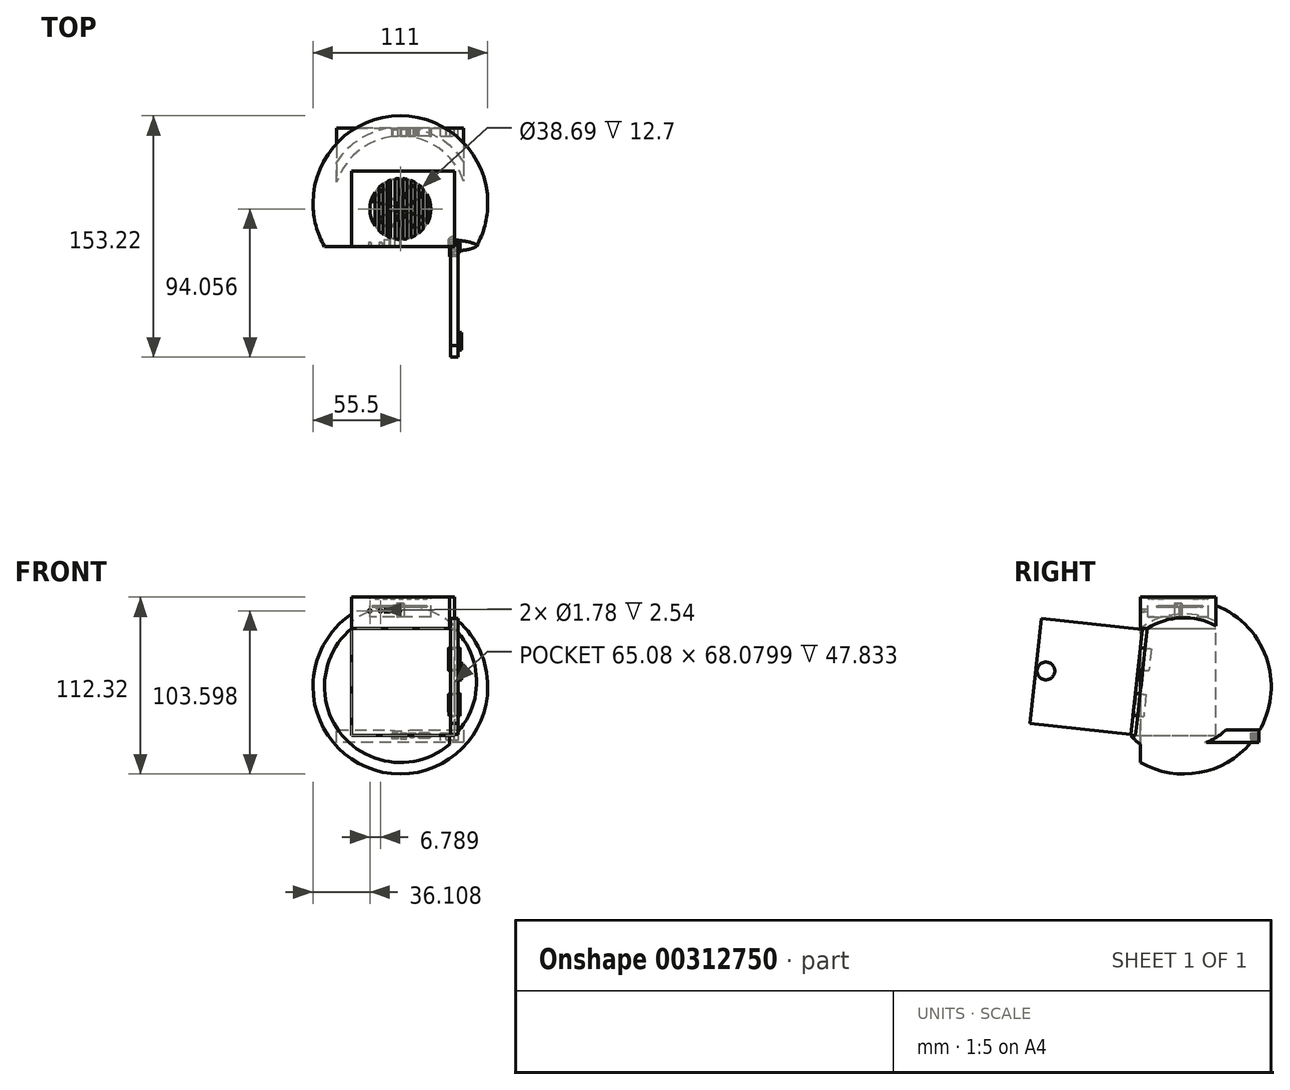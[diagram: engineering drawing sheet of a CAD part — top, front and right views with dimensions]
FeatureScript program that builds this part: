
annotation { "Feature Type Name" : "Feature", "Feature Type Description" : "" }
export const myFeature = defineFeature(function(context is Context, id is Id, definition is map)
    precondition{}
    {
        {
            var Q0;
            Q0=qCreatedBy(makeId("Front.planeOp"),FACE);
            var sketch = newSketch(context, id + "F0", { "sketchPlane" : qUnion([Q0])});
            skArc(sketch, "E0", {"start": v(55.5, 0) * mm, "mid": v(0, 55.5) * mm, "end": v(-55.5, 0) * mm});
            skLineSegment(sketch, "E1", {"start": v(-55.5, 0) * mm, "end": v(55.5, 0) * mm});
            skSolve(sketch);
        }
        {
            var Q0;
            Q0 = qSketchRegion(id + "F0", true);
            var Q1;
            Q1=sQuery(id+"F0.wireOp",EDGE,"E1");
            revolve(context, id + "F1", {"entities" : qUnion([Q0]), "axis" : qUnion([Q1]), "revolveType" : RevolveType.FULL});
        }
        {
            var Q0;
            Q0=qCreatedBy(makeId("Front.planeOp"),FACE);
            var sketch = newSketch(context, id + "F2", { "sketchPlane" : qUnion([Q0])});
            skLineSegment(sketch, "E2", {"start": v(-30.83, 37.01) * mm, "end": v(34.25, 37.01) * mm});
            skLineSegment(sketch, "E3", {"start": v(34.25, 37.01) * mm, "end": v(34.25, -31.07) * mm});
            skLineSegment(sketch, "E4", {"start": v(34.25, -31.07) * mm, "end": v(-30.83, -31.07) * mm});
            skLineSegment(sketch, "E5", {"start": v(-30.83, -31.07) * mm, "end": v(-30.83, 37.01) * mm});
            skLineSegment(sketch, "E6", {"start": v(-56.39, 0) * mm, "end": v(59.8, 0) * mm});
            skSolve(sketch);
        }
        {
            var Q0;
            Q0=qCreatedBy(makeId("Front.planeOp"),FACE);
            var sketch = newSketch(context, id + "F3", { "sketchPlane" : qUnion([Q0])});
            skLineSegment(sketch, "E7", {"start": v(40.18, -35.57) * mm, "end": v(-40.42, -35.57) * mm});
            skLineSegment(sketch, "E8", {"start": v(-40.42, -35.57) * mm, "end": v(-40.42, -27.54) * mm});
            skLineSegment(sketch, "E9", {"start": v(-40.42, -27.54) * mm, "end": v(40.18, -27.54) * mm});
            skLineSegment(sketch, "E10", {"start": v(40.18, -27.54) * mm, "end": v(40.18, -35.57) * mm});
            skSolve(sketch);
        }
        {
            var Q0;
            Q0 = qSketchRegion(id + "F3", true);
            extrude(context, id + "F4", {"entities" : qUnion([Q0]), "operationType" : NewBodyOperationType.ADD, "oppositeDirection" : true, "depth" : 47.75 * mm});
        }
        {
            var Q0;
            Q0=makeQuery(id+"F4.opExtrude","CAP_FACE",FACE,{"disambiguationData":[OSD([sQuery(id+"F3.wireOp",EDGE,"E7"),sQuery(id+"F3.wireOp",EDGE,"E8"),sQuery(id+"F3.wireOp",EDGE,"E9"),sQuery(id+"F3.wireOp",EDGE,"E10")])],"isStart":false});
            var sketch = newSketch(context, id + "F5", { "sketchPlane" : qUnion([Q0])});
            skLineSegment(sketch, "E11", {"start": v(-36.59, -29.3) * mm, "end": v(-36.59, -34.19) * mm});
            skLineSegment(sketch, "E12", {"start": v(-36.59, -34.19) * mm, "end": v(-25.65, -34.19) * mm});
            skLineSegment(sketch, "E13", {"start": v(-25.65, -34.19) * mm, "end": v(-25.65, -29.3) * mm});
            skLineSegment(sketch, "E14", {"start": v(-25.65, -29.3) * mm, "end": v(-36.59, -29.3) * mm});
            skLineSegment(sketch, "E15", {"start": v(-18.62, -29.3) * mm, "end": v(-11.86, -29.3) * mm});
            skLineSegment(sketch, "E16", {"start": v(-11.86, -29.3) * mm, "end": v(-11.86, -30.02) * mm});
            skLineSegment(sketch, "E17", {"start": v(-18.62, -29.3) * mm, "end": v(-18.62, -30.02) * mm});
            skLineSegment(sketch, "E18.MirrorCS", {"start": v(-18.62, -32.85) * mm, "end": v(-18.62, -32.11) * mm});
            skLineSegment(sketch, "E19.MirrorCS", {"start": v(-18.62, -32.85) * mm, "end": v(-11.86, -32.85) * mm});
            skLineSegment(sketch, "E20.MirrorCS", {"start": v(-11.86, -32.85) * mm, "end": v(-11.86, -32.11) * mm});
            skArc(sketch, "E21", {"start": v(-18.62, -30.02) * mm, "mid": v(-19.7, -31.07) * mm, "end": v(-18.62, -32.11) * mm});
            skArc(sketch, "E22", {"start": v(-11.86, -32.11) * mm, "mid": v(-10.83, -31.07) * mm, "end": v(-11.86, -30.02) * mm});
            skLineSegment(sketch, "E23", {"start": v(-9.63, -29.3) * mm, "end": v(-9.63, -31.07) * mm});
            skLineSegment(sketch, "E24", {"start": v(-9.63, -31.07) * mm, "end": v(-8.36, -31.07) * mm});
            skLineSegment(sketch, "E25", {"start": v(-8.36, -31.07) * mm, "end": v(-8.36, -32.5) * mm});
            skLineSegment(sketch, "E26", {"start": v(-8.36, -32.5) * mm, "end": v(-6.57, -32.5) * mm});
            skLineSegment(sketch, "E27", {"start": v(-6.57, -32.5) * mm, "end": v(-6.57, -31.07) * mm});
            skLineSegment(sketch, "E28", {"start": v(-6.57, -31.07) * mm, "end": v(-5.3, -31.07) * mm});
            skLineSegment(sketch, "E29", {"start": v(-5.3, -31.07) * mm, "end": v(-5.3, -29.3) * mm});
            skLineSegment(sketch, "E30", {"start": v(-5.3, -29.3) * mm, "end": v(-9.63, -29.3) * mm});
            skLineSegment(sketch, "E31", {"start": v(-3.85, -29.3) * mm, "end": v(-3.85, -31.07) * mm});
            skLineSegment(sketch, "E32", {"start": v(-3.85, -31.07) * mm, "end": v(0, -31.07) * mm});
            skLineSegment(sketch, "E33", {"start": v(0, -31.07) * mm, "end": v(0, -29.3) * mm});
            skLineSegment(sketch, "E34", {"start": v(0, -29.3) * mm, "end": v(-3.85, -29.3) * mm});
            skLineSegment(sketch, "E35", {"start": v(1.49, -31.07) * mm, "end": v(1.49, -29.3) * mm});
            skLineSegment(sketch, "E36", {"start": v(1.49, -29.3) * mm, "end": v(5.28, -29.3) * mm});
            skLineSegment(sketch, "E37", {"start": v(5.28, -29.3) * mm, "end": v(5.28, -31.07) * mm});
            skLineSegment(sketch, "E38", {"start": v(5.28, -31.07) * mm, "end": v(1.49, -31.07) * mm});
            skLineSegment(sketch, "E39", {"start": v(-3.85, -31.55) * mm, "end": v(0, -31.55) * mm});
            skLineSegment(sketch, "E40", {"start": v(0, -31.55) * mm, "end": v(0, -33.32) * mm});
            skLineSegment(sketch, "E41", {"start": v(0, -33.32) * mm, "end": v(-3.85, -33.32) * mm});
            skLineSegment(sketch, "E42", {"start": v(-3.85, -33.32) * mm, "end": v(-3.85, -31.55) * mm});
            skLineSegment(sketch, "E43", {"start": v(1.49, -31.55) * mm, "end": v(1.49, -33.32) * mm});
            skLineSegment(sketch, "E44", {"start": v(1.49, -33.32) * mm, "end": v(5.28, -33.32) * mm});
            skLineSegment(sketch, "E45", {"start": v(5.28, -33.32) * mm, "end": v(5.28, -31.55) * mm});
            skLineSegment(sketch, "E46", {"start": v(5.28, -31.55) * mm, "end": v(1.49, -31.55) * mm});
            skSolve(sketch);
        }
        {
            var Q0;
            Q0 = qSketchRegion(id + "F5", true);
            extrude(context, id + "F6", {"entities" : qUnion([Q0]), "operationType" : NewBodyOperationType.REMOVE, "oppositeDirection" : true, "depth" : 5.08 * mm});
        }
        {
            var Q0;
            Q0=makeQuery(id+"F6.boolean.opBoolean","COPY",FACE,{"derivedFrom":makeQuery(id+"F6.opExtrude","CAP_FACE",FACE,{"disambiguationData":[OSD([sQuery(id+"F5.wireOp",EDGE,"E11"),sQuery(id+"F5.wireOp",EDGE,"E12"),sQuery(id+"F5.wireOp",EDGE,"E13"),sQuery(id+"F5.wireOp",EDGE,"E14")])],"isStart":false})});
            var sketch = newSketch(context, id + "F7", { "sketchPlane" : qUnion([Q0])});
            skLineSegment(sketch, "E47.bottom", {"start": v(-34.22, -32.3) * mm, "end": v(-33.71, -32.3) * mm});
            skLineSegment(sketch, "E47.top", {"start": v(-34.22, -33.57) * mm, "end": v(-33.71, -33.57) * mm});
            skLineSegment(sketch, "E47.left", {"start": v(-34.22, -32.3) * mm, "end": v(-34.22, -33.57) * mm});
            skLineSegment(sketch, "E47.right", {"start": v(-33.71, -32.3) * mm, "end": v(-33.71, -33.57) * mm});
            skLineSegment(sketch, "E48.bottom", {"start": v(-31.68, -30.65) * mm, "end": v(-31.17, -30.65) * mm});
            skLineSegment(sketch, "E48.top", {"start": v(-31.68, -31.92) * mm, "end": v(-31.17, -31.92) * mm});
            skLineSegment(sketch, "E48.left", {"start": v(-31.68, -30.65) * mm, "end": v(-31.68, -31.92) * mm});
            skLineSegment(sketch, "E48.right", {"start": v(-31.17, -30.65) * mm, "end": v(-31.17, -31.92) * mm});
            skLineSegment(sketch, "E49.bottom", {"start": v(-29.14, -32.3) * mm, "end": v(-28.63, -32.3) * mm});
            skLineSegment(sketch, "E49.top", {"start": v(-29.14, -33.57) * mm, "end": v(-28.63, -33.57) * mm});
            skLineSegment(sketch, "E49.left", {"start": v(-29.14, -32.3) * mm, "end": v(-29.14, -33.57) * mm});
            skLineSegment(sketch, "E49.right", {"start": v(-28.63, -32.3) * mm, "end": v(-28.63, -33.57) * mm});
            skLineSegment(sketch, "E50.bottom", {"start": v(-3.55, -33.02) * mm, "end": v(-0.3, -33.02) * mm});
            skLineSegment(sketch, "E50.top", {"start": v(-3.55, -32.77) * mm, "end": v(-0.3, -32.77) * mm});
            skLineSegment(sketch, "E50.left", {"start": v(-3.55, -33.02) * mm, "end": v(-3.55, -32.77) * mm});
            skLineSegment(sketch, "E50.right", {"start": v(-0.3, -33.02) * mm, "end": v(-0.3, -32.77) * mm});
            skLineSegment(sketch, "E51", {"start": v(-3.55, -30.76) * mm, "end": v(-0.3, -30.76) * mm});
            skLineSegment(sketch, "E52", {"start": v(-0.3, -30.76) * mm, "end": v(-0.3, -30.51) * mm});
            skLineSegment(sketch, "E53", {"start": v(-0.3, -30.51) * mm, "end": v(-3.55, -30.51) * mm});
            skLineSegment(sketch, "E54", {"start": v(-3.55, -30.51) * mm, "end": v(-3.55, -30.76) * mm});
            skLineSegment(sketch, "E55", {"start": v(1.8, -30.51) * mm, "end": v(1.8, -30.76) * mm});
            skLineSegment(sketch, "E56", {"start": v(1.8, -30.76) * mm, "end": v(4.98, -30.76) * mm});
            skLineSegment(sketch, "E57", {"start": v(4.98, -30.76) * mm, "end": v(4.98, -30.51) * mm});
            skLineSegment(sketch, "E58", {"start": v(4.98, -30.51) * mm, "end": v(1.8, -30.51) * mm});
            skLineSegment(sketch, "E59", {"start": v(1.8, -32.77) * mm, "end": v(4.98, -32.77) * mm});
            skLineSegment(sketch, "E60", {"start": v(4.98, -32.77) * mm, "end": v(4.98, -33.02) * mm});
            skLineSegment(sketch, "E61", {"start": v(4.98, -33.02) * mm, "end": v(1.8, -33.02) * mm});
            skLineSegment(sketch, "E62", {"start": v(1.8, -33.02) * mm, "end": v(1.8, -32.77) * mm});
            skSolve(sketch);
        }
        {
            var Q0;
            Q0 = qSketchRegion(id + "F7", true);
            extrude(context, id + "F8", {"entities" : qUnion([Q0]), "operationType" : NewBodyOperationType.ADD, "depth" : 4.2 * mm});
        }
        {
            var Q0;
            Q0 = qSketchRegion(id + "F2", true);
            extrude(context, id + "F9", {"entities" : qUnion([Q0]), "operationType" : NewBodyOperationType.REMOVE, "depth" : 68.07 * mm});
        }
        {
            var Q0;
            Q0=makeQuery(id+"F9.boolean.opBoolean","COPY",FACE,{"derivedFrom":makeQuery(id+"F9.opExtrude","CAP_FACE",FACE,{"disambiguationData":[OSD([sQuery(id+"F2.wireOp",EDGE,"E2"),sQuery(id+"F2.wireOp",EDGE,"E3"),sQuery(id+"F2.wireOp",EDGE,"E4"),sQuery(id+"F2.wireOp",EDGE,"E5")])],"isStart":true})});
            var sketch = newSketch(context, id + "F10", { "sketchPlane" : qUnion([Q0])});
            skLineSegment(sketch, "E63.0", {"start": v(-30.83, 37.01) * mm, "end": v(34.25, 37.01) * mm});
            skLineSegment(sketch, "E63.1", {"start": v(34.25, 37.01) * mm, "end": v(34.25, -31.07) * mm});
            skLineSegment(sketch, "E63.2", {"start": v(34.25, -31.07) * mm, "end": v(-30.83, -31.07) * mm});
            skLineSegment(sketch, "E63.3", {"start": v(-30.83, -31.07) * mm, "end": v(-30.83, 37.01) * mm});
            skSolve(sketch);
        }
        {
            var Q0;
            Q0 = qSketchRegion(id + "F10", true);
            extrude(context, id + "F11", {"entities" : qUnion([Q0]), "operationType" : NewBodyOperationType.REMOVE, "oppositeDirection" : true, "depth" : 20.32 * mm});
        }
        {
            var Q0;
            Q0=makeQuery(id+"F11.boolean.opBoolean","MERGE",FACE,{"derivedFrom":[makeQuery(id+"F9.boolean.opBoolean","COPY",FACE,{"derivedFrom":makeQuery(id+"F9.opExtrude","SWEPT_FACE",FACE,{"disambiguationData":[OSD([sQuery(id+"F2.wireOp",EDGE,"E2")])]})}),makeQuery(id+"F11.opExtrude","SWEPT_FACE",FACE,{"disambiguationData":[OSD([sQuery(id+"F10.wireOp",EDGE,"E63.0")])]})]});
            var sketch = newSketch(context, id + "F12", { "sketchPlane" : qUnion([Q0])});
            skLineSegment(sketch, "E64.bottom", {"start": v(-30.83, 27.56) * mm, "end": v(34.25, 27.56) * mm});
            skLineSegment(sketch, "E64.top", {"start": v(-30.83, -20.32) * mm, "end": v(34.25, -20.32) * mm});
            skLineSegment(sketch, "E64.left", {"start": v(-30.83, 27.56) * mm, "end": v(-30.83, -20.32) * mm});
            skLineSegment(sketch, "E64.right", {"start": v(34.25, 27.56) * mm, "end": v(34.25, -20.32) * mm});
            skSolve(sketch);
        }
        {
            var Q0;
            Q0 = qSketchRegion(id + "F12", true);
            extrude(context, id + "F13", {"entities" : qUnion([Q0]), "operationType" : NewBodyOperationType.ADD, "oppositeDirection" : true, "depth" : 18.54 * mm});
        }
        {
            var Q0;
            Q0=makeQuery(id+"F13.opExtrude","CAP_FACE",FACE,{"disambiguationData":[OSD([sQuery(id+"F12.wireOp",EDGE,"E64.bottom"),sQuery(id+"F12.wireOp",EDGE,"E64.top"),sQuery(id+"F12.wireOp",EDGE,"E64.left"),sQuery(id+"F12.wireOp",EDGE,"E64.right")])],"isStart":false});
            var sketch = newSketch(context, id + "F14", { "sketchPlane" : qUnion([Q0])});
            skCircle(sketch, "E65", {"center": v(0, -3.66) * mm, "radius": 19.34 * mm});
            skSolve(sketch);
        }
        {
            var Q0;
            Q0 = qSketchRegion(id + "F14", true);
            extrude(context, id + "F15", {"entities" : qUnion([Q0]), "operationType" : NewBodyOperationType.REMOVE, "oppositeDirection" : true, "depth" : 11.43 * mm});
        }
        {
            var Q0;
            Q0=makeQuery(id+"F15.boolean.opBoolean","COPY",FACE,{"derivedFrom":makeQuery(id+"F15.opExtrude","CAP_FACE",FACE,{"disambiguationData":[OSD([sQuery(id+"F14.wireOp",EDGE,"E65")])],"isStart":false})});
            var sketch = newSketch(context, id + "F16", { "sketchPlane" : qUnion([Q0])});
            skCircle(sketch, "E66", {"center": v(0, -3.66) * mm, "radius": 2.33 * mm});
            skSolve(sketch);
        }
        {
            var Q0;
            Q0 = qSketchRegion(id + "F16", true);
            extrude(context, id + "F17", {"entities" : qUnion([Q0]), "operationType" : NewBodyOperationType.ADD, "depth" : 8.64 * mm});
        }
        {
            var Q0;
            Q0=makeQuery(id+"F15.boolean.opBoolean","COPY",FACE,{"derivedFrom":makeQuery(id+"F15.opExtrude","CAP_FACE",FACE,{"disambiguationData":[OSD([sQuery(id+"F14.wireOp",EDGE,"E65")])],"isStart":false})});
            var sketch = newSketch(context, id + "F18", { "sketchPlane" : qUnion([Q0])});
            skLineSegment(sketch, "E67", {"start": v(0, -1.34) * mm, "end": v(6.53, 12.23) * mm});
            skLineSegment(sketch, "E68", {"start": v(6.53, 12.23) * mm, "end": v(14.72, 4.96) * mm});
            skLineSegment(sketch, "E69", {"start": v(14.72, 4.96) * mm, "end": v(2.29, -3.23) * mm});
            skLineSegment(sketch, "E70", {"start": v(0, -6) * mm, "end": v(-7, -17.44) * mm});
            skLineSegment(sketch, "E71", {"start": v(-7, -17.44) * mm, "end": v(-14.2, -9.67) * mm});
            skLineSegment(sketch, "E72", {"start": v(-14.2, -9.67) * mm, "end": v(-2.33, -3.66) * mm});
            skLineSegment(sketch, "E73", {"start": v(-2.06, -2.58) * mm, "end": v(-18.04, 1.03) * mm});
            skLineSegment(sketch, "E74", {"start": v(-18.04, 1.03) * mm, "end": v(-10.77, 9.55) * mm});
            skLineSegment(sketch, "E75", {"start": v(-10.77, 9.55) * mm, "end": v(-1.2, -1.67) * mm});
            skLineSegment(sketch, "E76", {"start": v(2.05, -4.77) * mm, "end": v(16.8, -9.92) * mm});
            skLineSegment(sketch, "E77", {"start": v(16.8, -9.92) * mm, "end": v(9.54, -16.44) * mm});
            skLineSegment(sketch, "E78", {"start": v(9.54, -16.44) * mm, "end": v(1.06, -5.74) * mm});
            skArc(sketch, "E79", {"start": v(2.29, -3.23) * mm, "mid": v(1.44, -1.92) * mm, "end": v(0, -1.34) * mm});
            skArc(sketch, "E80", {"start": v(1.06, -5.74) * mm, "mid": v(1.65, -5.35) * mm, "end": v(2.05, -4.77) * mm});
            skArc(sketch, "E81", {"start": v(-2.33, -3.66) * mm, "mid": v(-1.65, -5.31) * mm, "end": v(0, -6) * mm});
            skArc(sketch, "E82", {"start": v(-1.2, -1.67) * mm, "mid": v(-1.69, -2.07) * mm, "end": v(-2.06, -2.58) * mm});
            skSolve(sketch);
        }
        {
            var Q0;
            Q0 = qSketchRegion(id + "F18", true);
            extrude(context, id + "F19", {"entities" : qUnion([Q0]), "depth" : 7.11 * mm});
        }
        {
            var Q0;
            Q0=makeQuery(id+"F15.boolean.opBoolean","COPY",FACE,{"derivedFrom":makeQuery(id+"F15.opExtrude","CAP_FACE",FACE,{"disambiguationData":[OSD([sQuery(id+"F14.wireOp",EDGE,"E65")])],"isStart":false})});
            var sketch = newSketch(context, id + "F20", { "sketchPlane" : qUnion([Q0])});
            skCircle(sketch, "E83", {"center": v(0, -3.66) * mm, "radius": 19.26 * mm});
            skCircle(sketch, "E84", {"center": v(0, -3.66) * mm, "radius": 2.32 * mm});
            skSolve(sketch);
        }
        {
            var Q0;
            Q0 = qSketchRegion(id + "F20", true);
            extrude(context, id + "F21", {"entities" : qUnion([Q0]), "operationType" : NewBodyOperationType.REMOVE, "depth" : 6.6 * mm});
        }
        {
            var Q0;
            Q0=makeQuery(id+"F13.opExtrude","CAP_FACE",FACE,{"disambiguationData":[OSD([sQuery(id+"F12.wireOp",EDGE,"E64.bottom"),sQuery(id+"F12.wireOp",EDGE,"E64.top"),sQuery(id+"F12.wireOp",EDGE,"E64.left"),sQuery(id+"F12.wireOp",EDGE,"E64.right")])],"isStart":false});
            var sketch = newSketch(context, id + "F22", { "sketchPlane" : qUnion([Q0])});
            skLineSegment(sketch, "E85.bottom", {"start": v(-8.45, 17.37) * mm, "end": v(-11, 17.37) * mm});
            skLineSegment(sketch, "E85.top", {"start": v(-8.45, -22.19) * mm, "end": v(-11, -22.19) * mm});
            skLineSegment(sketch, "E85.left", {"start": v(-8.45, 17.37) * mm, "end": v(-8.45, -22.19) * mm});
            skLineSegment(sketch, "E85.right", {"start": v(-11, 17.37) * mm, "end": v(-11, -22.19) * mm});
            skLineSegment(sketch, "E86.bottom", {"start": v(11.87, 17.37) * mm, "end": v(9.33, 17.37) * mm});
            skLineSegment(sketch, "E86.top", {"start": v(11.87, -22.19) * mm, "end": v(9.33, -22.19) * mm});
            skLineSegment(sketch, "E86.left", {"start": v(11.87, 17.37) * mm, "end": v(11.87, -22.19) * mm});
            skLineSegment(sketch, "E86.right", {"start": v(9.33, 17.37) * mm, "end": v(9.33, -22.19) * mm});
            skLineSegment(sketch, "E87.bottom", {"start": v(6.79, 17.37) * mm, "end": v(4.25, 17.37) * mm});
            skLineSegment(sketch, "E87.top", {"start": v(6.79, -23.46) * mm, "end": v(4.25, -23.46) * mm});
            skLineSegment(sketch, "E87.left", {"start": v(6.79, 17.37) * mm, "end": v(6.79, -23.46) * mm});
            skLineSegment(sketch, "E87.right", {"start": v(4.25, 17.37) * mm, "end": v(4.25, -23.46) * mm});
            skLineSegment(sketch, "E88.bottom", {"start": v(-6.24, 17.37) * mm, "end": v(-3.37, 17.37) * mm});
            skLineSegment(sketch, "E88.top", {"start": v(-6.24, -23.46) * mm, "end": v(-3.37, -23.46) * mm});
            skLineSegment(sketch, "E88.left", {"start": v(-6.24, 17.37) * mm, "end": v(-6.24, -23.46) * mm});
            skLineSegment(sketch, "E88.right", {"start": v(-3.37, 17.37) * mm, "end": v(-3.37, -23.46) * mm});
            skPoint(sketch, "E89.oppositeSnap0", {"position": v(1.7, -27.56) * mm});
            skLineSegment(sketch, "E89.bottom", {"start": v(-0.83, 17.37) * mm, "end": v(1.7, 17.37) * mm});
            skLineSegment(sketch, "E89.top", {"start": v(-0.83, -25.42) * mm, "end": v(1.7, -25.42) * mm});
            skLineSegment(sketch, "E89.left", {"start": v(-0.83, 17.37) * mm, "end": v(-0.83, -25.42) * mm});
            skLineSegment(sketch, "E89.right", {"start": v(1.7, 17.37) * mm, "end": v(1.7, -25.42) * mm});
            skLineSegment(sketch, "E90.bottom", {"start": v(14.4, 17.37) * mm, "end": v(16.93, 17.37) * mm});
            skLineSegment(sketch, "E90.top", {"start": v(14.4, -20.92) * mm, "end": v(16.93, -20.92) * mm});
            skLineSegment(sketch, "E90.left", {"start": v(14.4, 17.37) * mm, "end": v(14.4, -20.92) * mm});
            skLineSegment(sketch, "E90.right", {"start": v(16.93, 17.37) * mm, "end": v(16.93, -20.92) * mm});
            skPoint(sketch, "E91.oppositeSnap0", {"position": v(15.67, -20.92) * mm});
            skLineSegment(sketch, "E91.bottom", {"start": v(-13.53, 17.37) * mm, "end": v(-16.07, 17.37) * mm});
            skLineSegment(sketch, "E91.top", {"start": v(-13.53, -20.92) * mm, "end": v(-16.07, -20.92) * mm});
            skLineSegment(sketch, "E91.left", {"start": v(-13.53, 17.37) * mm, "end": v(-13.53, -20.92) * mm});
            skLineSegment(sketch, "E91.right", {"start": v(-16.07, 17.37) * mm, "end": v(-16.07, -20.92) * mm});
            skSolve(sketch);
        }
        {
            var Q0;
            Q0 = qSketchRegion(id + "F22", true);
            extrude(context, id + "F23", {"entities" : qUnion([Q0]), "operationType" : NewBodyOperationType.ADD, "depth" : 1.27 * mm});
        }
        {
            var Q0;
            Q0=qCreatedBy(makeId("Right.planeOp"),FACE);
            var sketch = newSketch(context, id + "F24", { "sketchPlane" : qUnion([Q0])});
            skArc(sketch, "E92.0", {"start": v(-23.19, 37.01) * mm, "mid": v(-43.41, 4.79) * mm, "end": v(-30.7, -31.07) * mm});
            skLineSegment(sketch, "E93", {"start": v(-23.19, 37.01) * mm, "end": v(-30.7, -31.07) * mm});
            skSolve(sketch);
        }
        {
            var Q0;
            Q0 = qSketchRegion(id + "F24", true);
            extrude(context, id + "F25", {"entities" : qUnion([Q0]), "operationType" : NewBodyOperationType.REMOVE, "depth" : 85.85 * mm});
        }
        {
            var Q0;
            Q0=makeQuery(id+"F25.boolean.opBoolean","COPY",FACE,{"derivedFrom":makeQuery(id+"F25.opExtrude","SWEPT_FACE",FACE,{"disambiguationData":[OSD([sQuery(id+"F24.wireOp",EDGE,"E93")])]})});
            var sketch = newSketch(context, id + "F26", { "sketchPlane" : qUnion([Q0])});
            skLineSegment(sketch, "E94.bottom", {"start": v(34.25, 7.62) * mm, "end": v(38.06, 7.62) * mm});
            skLineSegment(sketch, "E94.top", {"start": v(34.25, 21.59) * mm, "end": v(38.06, 21.59) * mm});
            skLineSegment(sketch, "E94.left", {"start": v(34.25, 7.62) * mm, "end": v(34.25, 21.59) * mm});
            skLineSegment(sketch, "E94.right", {"start": v(38.06, 7.62) * mm, "end": v(38.06, 21.59) * mm});
            skLineSegment(sketch, "E95.bottom", {"start": v(34.25, -7.62) * mm, "end": v(38.06, -7.62) * mm});
            skLineSegment(sketch, "E95.top", {"start": v(34.25, -21.6) * mm, "end": v(38.06, -21.6) * mm});
            skLineSegment(sketch, "E95.left", {"start": v(34.25, -7.62) * mm, "end": v(34.25, -21.6) * mm});
            skLineSegment(sketch, "E95.right", {"start": v(38.06, -7.62) * mm, "end": v(38.06, -21.6) * mm});
            skSolve(sketch);
        }
        {
            var Q0;
            Q0 = qSketchRegion(id + "F26", true);
            var Q1;
            Q1=makeQuery(id+"F25.boolean.opBoolean","INTERSECT",EDGE,{"derivedFrom":[makeQuery(id+"F11.boolean.opBoolean","MERGE",FACE,{"derivedFrom":[makeQuery(id+"F9.boolean.opBoolean","COPY",FACE,{"derivedFrom":makeQuery(id+"F9.opExtrude","SWEPT_FACE",FACE,{"disambiguationData":[OSD([sQuery(id+"F2.wireOp",EDGE,"E3")])]})}),makeQuery(id+"F11.opExtrude","SWEPT_FACE",FACE,{"disambiguationData":[OSD([sQuery(id+"F10.wireOp",EDGE,"E63.1")])]})]}),makeQuery(id+"F25.opExtrude","SWEPT_FACE",FACE,{"disambiguationData":[OSD([sQuery(id+"F24.wireOp",EDGE,"E93")])]})]});
            revolve(context, id + "F27", {"operationType" : NewBodyOperationType.ADD, "entities" : qUnion([Q0]), "axis" : qUnion([Q1]), "revolveType" : RevolveType.FULL});
        }
        {
            var Q0;
            Q0=makeQuery(id+"F11.boolean.opBoolean","MERGE",FACE,{"derivedFrom":[makeQuery(id+"F9.boolean.opBoolean","COPY",FACE,{"derivedFrom":makeQuery(id+"F9.opExtrude","SWEPT_FACE",FACE,{"disambiguationData":[OSD([sQuery(id+"F2.wireOp",EDGE,"E5")])]})}),makeQuery(id+"F11.opExtrude","SWEPT_FACE",FACE,{"disambiguationData":[OSD([sQuery(id+"F10.wireOp",EDGE,"E63.3")])]})]});
            var sketch = newSketch(context, id + "F28", { "sketchPlane" : qUnion([Q0])});
            skLineSegment(sketch, "E96.0", {"start": v(-23.19, 37.01) * mm, "end": v(-30.7, -31.07) * mm});
            skLineSegment(sketch, "E97", {"start": v(-26.43, 34.5) * mm, "end": v(-32.88, -24.03) * mm});
            skLineSegment(sketch, "E98", {"start": v(-32.88, -24.03) * mm, "end": v(-37.59, -23.51) * mm});
            skLineSegment(sketch, "E99", {"start": v(-37.59, -23.51) * mm, "end": v(-31.7, 29.85) * mm});
            skLineSegment(sketch, "E100", {"start": v(-31.7, 29.85) * mm, "end": v(-26.43, 34.5) * mm});
            skSolve(sketch);
        }
        {
            var Q0;
            Q0 = qSketchRegion(id + "F28", true);
            extrude(context, id + "F29", {"entities" : qUnion([Q0]), "operationType" : NewBodyOperationType.REMOVE, "depth" : 89.92 * mm});
        }
        {
            var Q0;
            Q0=makeQuery(id+"F29.boolean.opBoolean","COPY",FACE,{"disambiguationData":[TD([makeQuery(id+"F27.opRevolve","SWEPT_FACE",FACE,{"disambiguationData":[OSD([sQuery(id+"F26.wireOp",EDGE,"E94.bottom")])]})])],"derivedFrom":makeQuery(id+"F29.opExtrude","SWEPT_FACE",FACE,{"disambiguationData":[OSD([sQuery(id+"F28.wireOp",EDGE,"E97")])]})});
            var sketch = newSketch(context, id + "F30", { "sketchPlane" : qUnion([Q0])});
            skLineSegment(sketch, "E101.bottom", {"start": v(31.83, 33.17) * mm, "end": v(36.66, 33.17) * mm});
            skLineSegment(sketch, "E101.top", {"start": v(31.83, -34) * mm, "end": v(36.66, -34) * mm});
            skLineSegment(sketch, "E101.left", {"start": v(31.83, 33.17) * mm, "end": v(31.83, -34) * mm});
            skLineSegment(sketch, "E101.right", {"start": v(36.66, 33.17) * mm, "end": v(36.66, -34) * mm});
            skSolve(sketch);
        }
        {
            var Q0;
            Q0 = qSketchRegion(id + "F30", true);
            extrude(context, id + "F31", {"entities" : qUnion([Q0]), "depth" : 64.52 * mm});
        }
        {
            var Q0;
            Q0=makeQuery(id+"F31.opExtrude","SWEPT_FACE",FACE,{"disambiguationData":[OSD([sQuery(id+"F30.wireOp",EDGE,"E101.right")])]});
            var sketch = newSketch(context, id + "F32", { "sketchPlane" : qUnion([Q0])});
            skCircle(sketch, "E102", {"center": v(-87.64, 9.95) * mm, "radius": 5.61 * mm});
            skPoint(sketch, "E102.centerSnap0", {"position": v(-94.04, 9.95) * mm});
            skSolve(sketch);
        }
        {
            var Q0;
            Q0 = qSketchRegion(id + "F32", true);
            extrude(context, id + "F33", {"entities" : qUnion([Q0]), "operationType" : NewBodyOperationType.ADD, "endBound" : BoundingType.SYMMETRIC, "depth" : 4.57 * mm});
        }
        {
            var Q0;
            Q0=qCreatedBy(makeId("Top.planeOp"),FACE);
            var sketch = newSketch(context, id + "F34", { "sketchPlane" : qUnion([Q0])});
            skLineSegment(sketch, "E103.bottom", {"start": v(-57.15, -27.51) * mm, "end": v(31.2, -27.51) * mm});
            skLineSegment(sketch, "E103.top", {"start": v(-57.15, -47.88) * mm, "end": v(31.2, -47.88) * mm});
            skLineSegment(sketch, "E103.left", {"start": v(-57.15, -27.51) * mm, "end": v(-57.15, -47.88) * mm});
            skLineSegment(sketch, "E103.right", {"start": v(31.2, -27.51) * mm, "end": v(31.2, -47.88) * mm});
            skSolve(sketch);
        }
        {
            var Q0;
            Q0 = qSketchRegion(id + "F34", true);
            extrude(context, id + "F35", {"entities" : qUnion([Q0]), "operationType" : NewBodyOperationType.REMOVE, "endBound" : BoundingType.SYMMETRIC, "oppositeDirection" : true, "depth" : 137.67 * mm});
        }
        {
            var Q0;
            Q0=makeQuery(id+"F35.boolean.opBoolean","COPY",FACE,{"disambiguationData":[TD([makeQuery(id+"F1.opRevolve","SWEPT_FACE",FACE,{"disambiguationData":[OSD([sQuery(id+"F0.wireOp",EDGE,"E0")])]})])],"derivedFrom":makeQuery(id+"F35.opExtrude","SWEPT_FACE",FACE,{"disambiguationData":[OSD([sQuery(id+"F34.wireOp",EDGE,"E103.bottom")])]})});
            var sketch = newSketch(context, id + "F36", { "sketchPlane" : qUnion([Q0])});
            skCircle(sketch, "E104", {"center": v(-19.4, 48.1) * mm, "radius": 0.89 * mm});
            skCircle(sketch, "E105", {"center": v(-12.6, 48.1) * mm, "radius": 0.89 * mm});
            skSolve(sketch);
        }
        {
            var Q0;
            Q0 = qSketchRegion(id + "F36", true);
            extrude(context, id + "F37", {"entities" : qUnion([Q0]), "operationType" : NewBodyOperationType.REMOVE, "oppositeDirection" : true, "depth" : 2.54 * mm});
        }
        {
            var Q0;
            Q0=makeQuery(id+"F13.opExtrude","CAP_FACE",FACE,{"disambiguationData":[OSD([sQuery(id+"F12.wireOp",EDGE,"E64.bottom"),sQuery(id+"F12.wireOp",EDGE,"E64.top"),sQuery(id+"F12.wireOp",EDGE,"E64.left"),sQuery(id+"F12.wireOp",EDGE,"E64.right")])],"isStart":false});
            extrude(context, id + "F38", {"entities" : qUnion([Q0]), "operationType" : NewBodyOperationType.ADD, "depth" : 1.27 * mm});
        }
        {
            var Q0;
            {var subQ0=sQuery(id+"F34.wireOp",EDGE,"E103.bottom");var subQ1=sQuery(id+"F12.wireOp",EDGE,"E64.right");var subQ2=sQuery(id+"F12.wireOp",EDGE,"E64.left");var subQ3=sQuery(id+"F12.wireOp",EDGE,"E64.top");var subQ4=sQuery(id+"F12.wireOp",EDGE,"E64.bottom");Q0=makeQuery(id+"F38.boolean.opBoolean","MERGE",FACE,{"derivedFrom":[makeQuery(id+"F35.boolean.opBoolean","COPY",FACE,{"disambiguationData":[TD([makeQuery(id+"F1.opRevolve","SWEPT_FACE",FACE,{"disambiguationData":[OSD([sQuery(id+"F0.wireOp",EDGE,"E0")])]})])],"derivedFrom":makeQuery(id+"F35.opExtrude","SWEPT_FACE",FACE,{"disambiguationData":[OSD([subQ0])]})}),makeQuery(id+"F38.opExtrude","SWEPT_FACE",FACE,{"disambiguationData":[OSD([subQ4,subQ3,subQ2,subQ1,subQ0])]})]});}
            var sketch = newSketch(context, id + "F39", { "sketchPlane" : qUnion([Q0])});
            skLineSegment(sketch, "E106.bottom", {"start": v(-10.43, 49.05) * mm, "end": v(-6.62, 49.05) * mm});
            skLineSegment(sketch, "E106.top", {"start": v(-10.43, 47.27) * mm, "end": v(-6.62, 47.27) * mm});
            skLineSegment(sketch, "E106.left", {"start": v(-10.43, 49.05) * mm, "end": v(-10.43, 47.27) * mm});
            skLineSegment(sketch, "E106.right", {"start": v(-6.62, 49.05) * mm, "end": v(-6.62, 47.27) * mm});
            skLineSegment(sketch, "E107.bottom", {"start": v(-3.8, 49.05) * mm, "end": v(0, 49.05) * mm});
            skLineSegment(sketch, "E107.top", {"start": v(-3.8, 47.27) * mm, "end": v(0, 47.27) * mm});
            skLineSegment(sketch, "E107.left", {"start": v(-3.8, 49.05) * mm, "end": v(-3.8, 47.27) * mm});
            skLineSegment(sketch, "E107.right", {"start": v(0, 49.05) * mm, "end": v(0, 47.27) * mm});
            skSolve(sketch);
        }
        {
            var Q0;
            Q0 = qSketchRegion(id + "F39", true);
            extrude(context, id + "F40", {"entities" : qUnion([Q0]), "operationType" : NewBodyOperationType.REMOVE, "oppositeDirection" : true, "depth" : 4.44 * mm});
        }
        {
            var Q0;
            Q0=makeQuery(id+"F40.boolean.opBoolean","COPY",FACE,{"derivedFrom":makeQuery(id+"F40.opExtrude","CAP_FACE",FACE,{"disambiguationData":[OSD([sQuery(id+"F39.wireOp",EDGE,"E106.bottom"),sQuery(id+"F39.wireOp",EDGE,"E106.top"),sQuery(id+"F39.wireOp",EDGE,"E106.left"),sQuery(id+"F39.wireOp",EDGE,"E106.right")])],"isStart":false})});
            var sketch = newSketch(context, id + "F41", { "sketchPlane" : qUnion([Q0])});
            skLineSegment(sketch, "E108.bottom", {"start": v(-10.12, 47.83) * mm, "end": v(-6.92, 47.83) * mm});
            skLineSegment(sketch, "E108.top", {"start": v(-10.12, 47.58) * mm, "end": v(-6.92, 47.58) * mm});
            skLineSegment(sketch, "E108.left", {"start": v(-10.12, 47.83) * mm, "end": v(-10.12, 47.58) * mm});
            skLineSegment(sketch, "E108.right", {"start": v(-6.92, 47.83) * mm, "end": v(-6.92, 47.58) * mm});
            skLineSegment(sketch, "E109.bottom", {"start": v(-3.5, 47.83) * mm, "end": v(-0.3, 47.83) * mm});
            skLineSegment(sketch, "E109.top", {"start": v(-3.5, 47.58) * mm, "end": v(-0.3, 47.58) * mm});
            skLineSegment(sketch, "E109.left", {"start": v(-3.5, 47.83) * mm, "end": v(-3.5, 47.58) * mm});
            skLineSegment(sketch, "E109.right", {"start": v(-0.3, 47.83) * mm, "end": v(-0.3, 47.58) * mm});
            skLineSegment(sketch, "E110.0.0", {"start": v(-1.8, -32.77) * mm, "end": v(-1.8, -33.02) * mm});
            skLineSegment(sketch, "E110.0.1", {"start": v(-1.8, -33.02) * mm, "end": v(-4.98, -33.02) * mm});
            skLineSegment(sketch, "E110.0.2", {"start": v(-4.98, -33.02) * mm, "end": v(-4.98, -32.77) * mm});
            skLineSegment(sketch, "E110.0.3", {"start": v(-4.98, -32.77) * mm, "end": v(-1.8, -32.77) * mm});
            skSolve(sketch);
        }
        {
            var Q0;
            Q0 = qSketchRegion(id + "F41", true);
            extrude(context, id + "F42", {"entities" : qUnion([Q0]), "operationType" : NewBodyOperationType.ADD, "depth" : 4.06 * mm});
        }
    });
